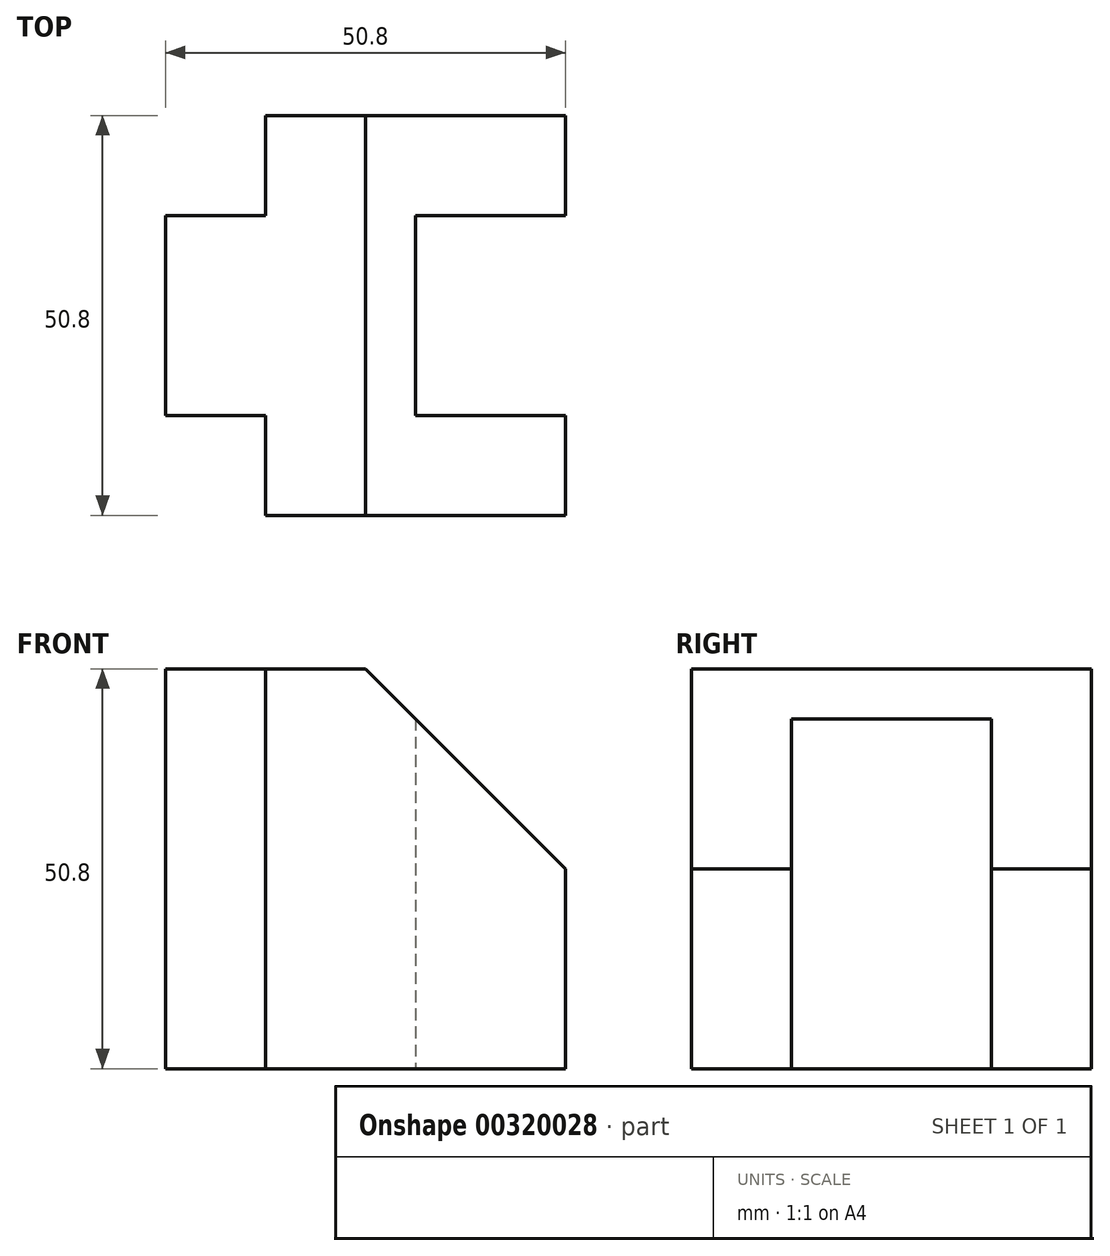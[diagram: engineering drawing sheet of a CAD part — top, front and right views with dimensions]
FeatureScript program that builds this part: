
annotation { "Feature Type Name" : "Feature", "Feature Type Description" : "" }
export const myFeature = defineFeature(function(context is Context, id is Id, definition is map)
    precondition{}
    {
        {
            var Q0;
            Q0=qCreatedBy(makeId("Front.planeOp"),FACE);
            var sketch = newSketch(context, id + "F0", { "sketchPlane" : qUnion([Q0])});
            skLineSegment(sketch, "E0.bottom", {"start": v(0, 0) * mm, "end": v(-25.4, 0) * mm});
            skLineSegment(sketch, "E0.top", {"start": v(0, 50.8) * mm, "end": v(-25.4, 50.8) * mm});
            skLineSegment(sketch, "E0.left", {"start": v(0, 0) * mm, "end": v(0, 50.8) * mm});
            skLineSegment(sketch, "E0.right", {"start": v(-25.4, 0) * mm, "end": v(-25.4, 50.8) * mm});
            skLineSegment(sketch, "E1", {"start": v(0, 0) * mm, "end": v(25.4, 0) * mm});
            skLineSegment(sketch, "E2", {"start": v(25.4, 0) * mm, "end": v(25.4, 25.4) * mm});
            skLineSegment(sketch, "E3", {"start": v(25.4, 25.4) * mm, "end": v(0, 50.8) * mm});
            skSolve(sketch);
        }
        {
            var Q0;
            Q0 = qSketchRegion(id + "F0", true);
            extrude(context, id + "F1", {"entities" : qUnion([Q0]), "endBound" : BoundingType.SYMMETRIC, "depth" : 50.8 * mm});
        }
        {
            var Q0;
            Q0=makeQuery(id+"F1.opExtrude","SWEPT_FACE",FACE,{"disambiguationData":[OSD([sQuery(id+"F0.wireOp",EDGE,"E0.bottom"),sQuery(id+"F0.wireOp",EDGE,"E1")])]});
            var sketch = newSketch(context, id + "F2", { "sketchPlane" : qUnion([Q0])});
            skLineSegment(sketch, "E4.bottom", {"start": v(25.4, -12.7) * mm, "end": v(6.35, -12.7) * mm});
            skLineSegment(sketch, "E4.top", {"start": v(25.4, 12.7) * mm, "end": v(6.35, 12.7) * mm});
            skLineSegment(sketch, "E4.left", {"start": v(25.4, -12.7) * mm, "end": v(25.4, 12.7) * mm});
            skLineSegment(sketch, "E4.right", {"start": v(6.35, -12.7) * mm, "end": v(6.35, 12.7) * mm});
            skLineSegment(sketch, "E5.bottom", {"start": v(-25.4, 25.4) * mm, "end": v(-12.7, 25.4) * mm});
            skLineSegment(sketch, "E5.top", {"start": v(-25.4, 12.7) * mm, "end": v(-12.7, 12.7) * mm});
            skLineSegment(sketch, "E5.left", {"start": v(-25.4, 25.4) * mm, "end": v(-25.4, 12.7) * mm});
            skLineSegment(sketch, "E5.right", {"start": v(-12.7, 25.4) * mm, "end": v(-12.7, 12.7) * mm});
            skLineSegment(sketch, "E6.bottom", {"start": v(-25.4, -25.4) * mm, "end": v(-12.7, -25.4) * mm});
            skLineSegment(sketch, "E6.top", {"start": v(-25.4, -12.7) * mm, "end": v(-12.7, -12.7) * mm});
            skLineSegment(sketch, "E6.left", {"start": v(-25.4, -25.4) * mm, "end": v(-25.4, -12.7) * mm});
            skLineSegment(sketch, "E6.right", {"start": v(-12.7, -25.4) * mm, "end": v(-12.7, -12.7) * mm});
            skSolve(sketch);
        }
        {
            var Q0;
            Q0 = qSketchRegion(id + "F2", true);
            extrude(context, id + "F3", {"entities" : qUnion([Q0]), "operationType" : NewBodyOperationType.REMOVE, "endBound" : BoundingType.THROUGH_ALL, "oppositeDirection" : true, "depth" : 25.4 * mm});
        }
    });
